# Revit family: 94895220novo
name_source: partatom
category: Equipamentos hidráulicos
revit_build: Autodesk Revit 2016 (Build: 20150220_1215(x64)
units: mm (PartAtom-declared; Revit-internal decimal feet)

## family parameters
Com base no plano de trabalho = Não
Compartilhado = Não
Corte com vazios quando carregados = Não
Cota do conector redondo = Utilizar diâmetro
Ponto de cálculo do ambiente = Não
Sempre na vertical = Sim
Tipo de parte = Normal

## types (1)
- Lava-louças 94895220
    Altura = 849mm
    Comentários de tipos = Ler Manual de Instalação
    Consumo de Agua = 2,52 Litros
    Consumo de Energia = 260,9 kWh
    Código de montagem = Lava-louças 94895220
    Descrição = Lava-louças 94895220
    Desenvolvedor = Factory Cursos & Desenvolvimento
    Fabricante = Tramontina
    Instalação - Nicho (Altura) = 851 mm
    Instalação - Nicho (Largura) = 600mm - Minimo
    Instalação - Nicho (Profundidade) = 570mm
    Largura = 599mm
    Modelo = Lava-louças 94895220
    Profundidade = 599mm
    Site do desenvolvedor = www.factorycursos.com.br
    Tampa = Sim
    Tipo de imagem = <Nenhum>
    URL = www.tramontina.com.br
